# Revit family: Hager-FW-IP44-With_Door-With_notch-sistema-NoHosted-PT-pt
name_source: partatom
category: Electrical Equipment
units: mm (PartAtom-declared; Revit-internal decimal feet)

## family parameters
Always vertical = Yes
Cut with Voids When Loaded = No
Panel Configuration = Two Columns, Circuits Across
Part Type = Panelboard
Room Calculation Point = No
Round Connector Dimension = Use Diameter
Shared = No
Work Plane-Based = Yes

## types (5) — shared parameters
Default Elevation = 1219 mm
EF000003 - Método de montagem = EV000128 - Parede oca
EF000007 - Cor = EV000202 - Branco
EF000008 - Largura = 603 mm
EF000049 - Profundidade = 112 mm  [stored 0.367454 ft]
EF000116 - Número RAL = 9010
EF000118 - Com tampa de montagem = No
EF000218 - Profundidade incorporada = 112 mm  [stored 0.367454 ft]
EF000339 - Tipo de difusor = EV005746 - Opcional
EF000846 - Largura para embutir = 603 mm
EF001062 - Versão EMC = No
EF001088 - Extensão possível = Yes
EF001131 - Profundidade interior = 112 mm  [stored 0.367454 ft]
EF001134 - Calha DIN = Yes
EF001596 - Material do corpo = EV000179 - Aço
EF002950 - Largura em número de módulos = 12
EF004462 - Tipo de fecho = EV000154 - Outro
EF005474 - Grau de proteção (IP) = EV006410 - IP30
EF006244 - Tampa/porta transparente = No
EF006306 - Com fecho = No
EF009212 - Tipo de tampa = EV009916 - Com recuo
EF015776 - Borne de terra = Yes
EF015777 - Borne de neutro = Yes
EF015941 - Porta para passagem de sinal = No
HG000001 - Número de colunas = 2
HG000002 - Com porta ou tampa = Yes
HG000003 - Gama = FW
HG000005 - Espessura = 3 mm  [stored 0.00984252 ft]
HG000006 - Encastrado = Yes
HG000009 - Porta dupla = No
HG000010 - Portas assimétricas = No
HG000011 - Filas vazias desde da parte de baixo = No
HG000017 - Distância entre polos = 18 mm  [stored 0.0590551 ft]
Manufacturer = Hager
Type Comments = FW
zero-valued in all types: HG000007 - Número de colunas vazias, HG000008 - Número de filas vazias

## per-type parameters (varying)
| type | EF000040 - Altura | EF000266 - Número de linhas | EF000332 - Altura embutida | HG000004 - Referência do Fabricante | Model |
| Montagem embutida IP30 L603 A1003 P112 12 unidade de divisão - FWU62GS | 1003 mm | 12 | 1003 mm | FWU62GS | FWU62GS |
| Montagem embutida IP30 L603 A1153 P112 12 unidade de divisão - FWU72GS | 1153 mm | 14 | 1153 mm | FWU72GS | FWU72GS |
| Montagem embutida IP30 L603 A553 P112 12 unidade de divisão - FWU32GS | 553 mm | 6 | 553 mm | FWU32GS | FWU32GS |
| Montagem embutida IP30 L603 A703 P112 12 unidade de divisão - FWU42GS | 703 mm | 8 | 703 mm | FWU42GS | FWU42GS |
| Montagem embutida IP30 L603 A853 P112 12 unidade de divisão - FWU52GS | 853 mm  [stored 2.79856 ft] | 10 | 853 mm  [stored 2.79856 ft] | FWU52GS | FWU52GS |

note: [stored X ft] marks values corroborated as IEEE doubles in the binary element streams (Revit-internal decimal feet)

## geometry (parser evidence)
native form markers: Sweep x13
no freeform markers — native parametric forms only
